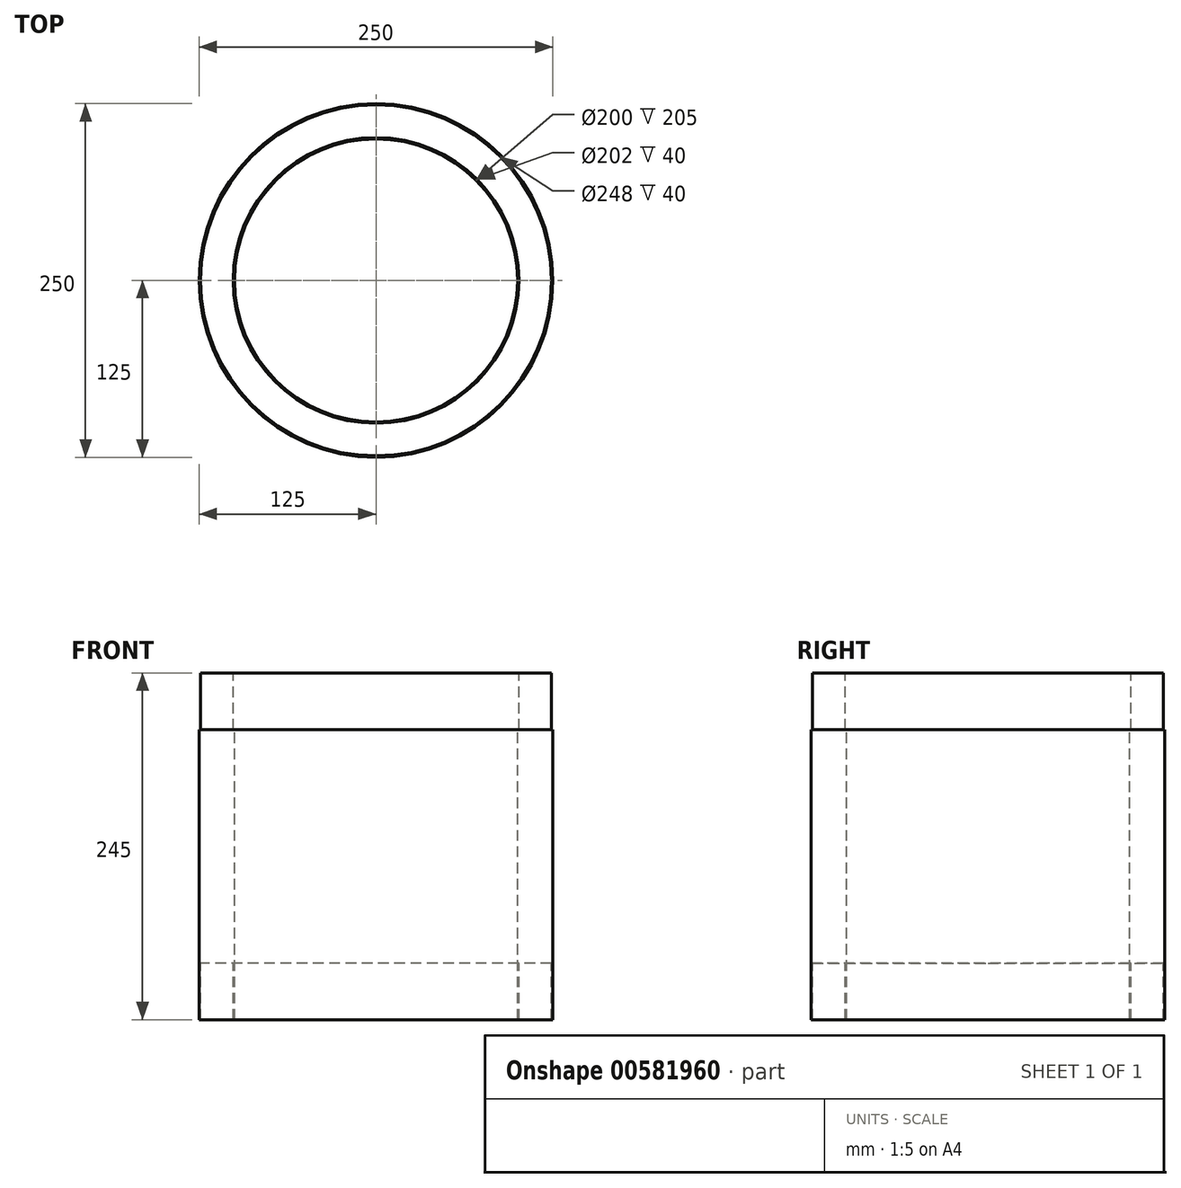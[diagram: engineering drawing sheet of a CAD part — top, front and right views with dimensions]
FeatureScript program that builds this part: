
annotation { "Feature Type Name" : "Feature", "Feature Type Description" : "" }
export const myFeature = defineFeature(function(context is Context, id is Id, definition is map)
    precondition{}
    {
        {
            var Q0;
            Q0=qCreatedBy(makeId("Front.planeOp"),FACE);
            var sketch = newSketch(context, id + "F0", { "sketchPlane" : qUnion([Q0])});
            skLineSegment(sketch, "E0", {"start": v(0, 345.75) * mm, "end": v(0, -558.03) * mm, "construction": true});
            skLineSegment(sketch, "E1", {"start": v(-100, -518.84) * mm, "end": v(-100, -313.84) * mm});
            skLineSegment(sketch, "E2", {"start": v(-100, -313.84) * mm, "end": v(-101, -313.84) * mm});
            skLineSegment(sketch, "E3", {"start": v(-101, -313.84) * mm, "end": v(-101, -273.84) * mm});
            skLineSegment(sketch, "E4", {"start": v(-101, -273.84) * mm, "end": v(-124, -273.84) * mm});
            skLineSegment(sketch, "E5", {"start": v(-124, -273.84) * mm, "end": v(-124, -313.84) * mm});
            skLineSegment(sketch, "E6", {"start": v(-124, -313.84) * mm, "end": v(-125, -313.84) * mm});
            skLineSegment(sketch, "E7", {"start": v(-125, -313.84) * mm, "end": v(-125, -518.84) * mm});
            skLineSegment(sketch, "E8", {"start": v(-125, -518.84) * mm, "end": v(-124, -518.84) * mm});
            skLineSegment(sketch, "E9", {"start": v(-124, -518.84) * mm, "end": v(-124, -478.84) * mm});
            skLineSegment(sketch, "E10", {"start": v(-124, -478.84) * mm, "end": v(-101, -478.84) * mm});
            skLineSegment(sketch, "E11", {"start": v(-101, -478.84) * mm, "end": v(-101, -518.84) * mm});
            skLineSegment(sketch, "E12", {"start": v(-101, -518.84) * mm, "end": v(-100, -518.84) * mm});
            skSolve(sketch);
        }
        {
            var Q0;
            Q0=qSketchRegion(id+"F0",true);
            var Q1;
            Q1=sQuery(id+"F0.wireOp",EDGE,"E0");
            revolve(context, id + "F1", {"entities" : qUnion([Q0]), "axis" : qUnion([Q1]), "revolveType" : RevolveType.FULL});
        }
    });
